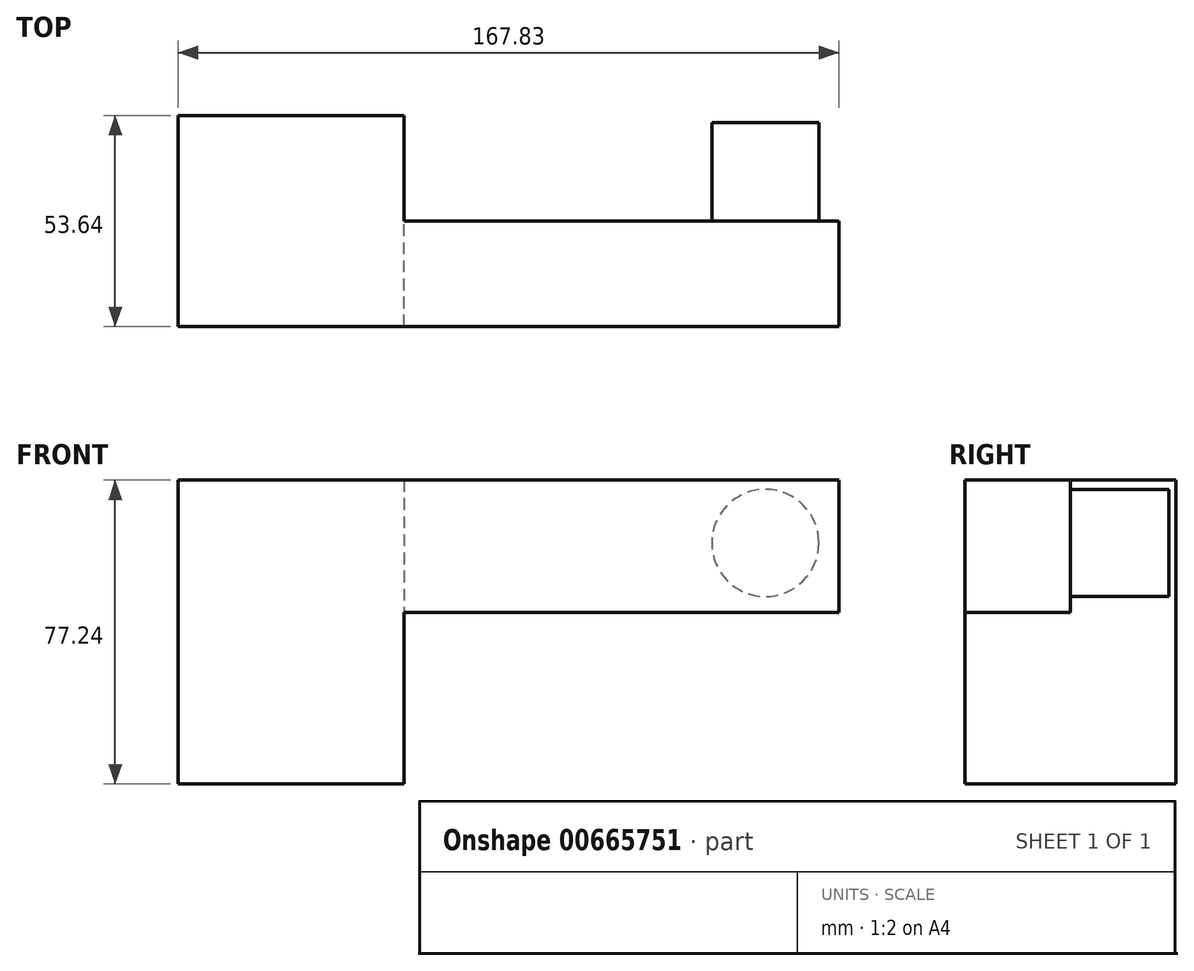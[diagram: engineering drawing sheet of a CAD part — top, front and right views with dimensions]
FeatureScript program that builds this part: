
annotation { "Feature Type Name" : "Feature", "Feature Type Description" : "" }
export const myFeature = defineFeature(function(context is Context, id is Id, definition is map)
    precondition{}
    {
        {
            var Q0;
            Q0=qCreatedBy(makeId("Top.planeOp"),FACE);
            var sketch = newSketch(context, id + "F0", { "sketchPlane" : qUnion([Q0])});
            skLineSegment(sketch, "E0.bottom", {"start": v(0, -53.64) * mm, "end": v(57.3, -53.64) * mm});
            skLineSegment(sketch, "E0.top", {"start": v(0, 0) * mm, "end": v(57.3, 0) * mm});
            skLineSegment(sketch, "E0.left", {"start": v(0, -53.64) * mm, "end": v(0, 0) * mm});
            skLineSegment(sketch, "E0.right", {"start": v(57.3, -53.64) * mm, "end": v(57.3, 0) * mm});
            skSolve(sketch);
        }
        {
            var Q0;
            Q0 = qSketchRegion(id + "F0", true);
            extrude(context, id + "F1", {"entities" : qUnion([Q0]), "depth" : 77.24 * mm, "offsetDistance" : 25.4 * mm});
        }
        {
            var Q0;
            Q0=makeQuery(id+"F1.opExtrude","SWEPT_FACE",FACE,{"disambiguationData":[OSD([sQuery(id+"F0.wireOp",EDGE,"E0.right")])]});
            var sketch = newSketch(context, id + "F2", { "sketchPlane" : qUnion([Q0])});
            skPoint(sketch, "E1.oppositeSnap0", {"position": v(-26.82, 77.24) * mm});
            skLineSegment(sketch, "E1.bottom", {"start": v(-53.64, 77.24) * mm, "end": v(-26.82, 77.24) * mm});
            skLineSegment(sketch, "E1.top", {"start": v(-53.64, 43.62) * mm, "end": v(-26.82, 43.62) * mm});
            skLineSegment(sketch, "E1.left", {"start": v(-53.64, 77.24) * mm, "end": v(-53.64, 43.62) * mm});
            skLineSegment(sketch, "E1.right", {"start": v(-26.82, 77.24) * mm, "end": v(-26.82, 43.62) * mm});
            skSolve(sketch);
        }
        {
            var Q0;
            Q0=makeQuery(id+"F2.imprint","IMPRINT",FACE,{"disambiguationData":[TD([[makeQuery(id+"F2.imprint","IMPRINT",EDGE,{"derivedFrom":sQuery(id+"F2.wireOp",EDGE,"E1.bottom")}),-1.0]])]});
            extrude(context, id + "F3", {"entities" : qUnion([Q0]), "operationType" : NewBodyOperationType.ADD, "depth" : 110.53 * mm, "offsetDistance" : 25.4 * mm});
        }
        {
            var Q0;
            Q0=makeQuery(id+"F3.opExtrude","SWEPT_FACE",FACE,{"disambiguationData":[OSD([sQuery(id+"F2.wireOp",EDGE,"E1.right")])]});
            var sketch = newSketch(context, id + "F4", { "sketchPlane" : qUnion([Q0])});
            skCircle(sketch, "E2", {"center": v(-149.15, 61.27) * mm, "radius": 13.61 * mm});
            skSolve(sketch);
        }
        {
            var Q0;
            Q0 = qSketchRegion(id + "F4", true);
            extrude(context, id + "F5", {"entities" : qUnion([Q0]), "operationType" : NewBodyOperationType.ADD, "depth" : 25 * mm, "offsetDistance" : 25 * mm});
        }
    });
